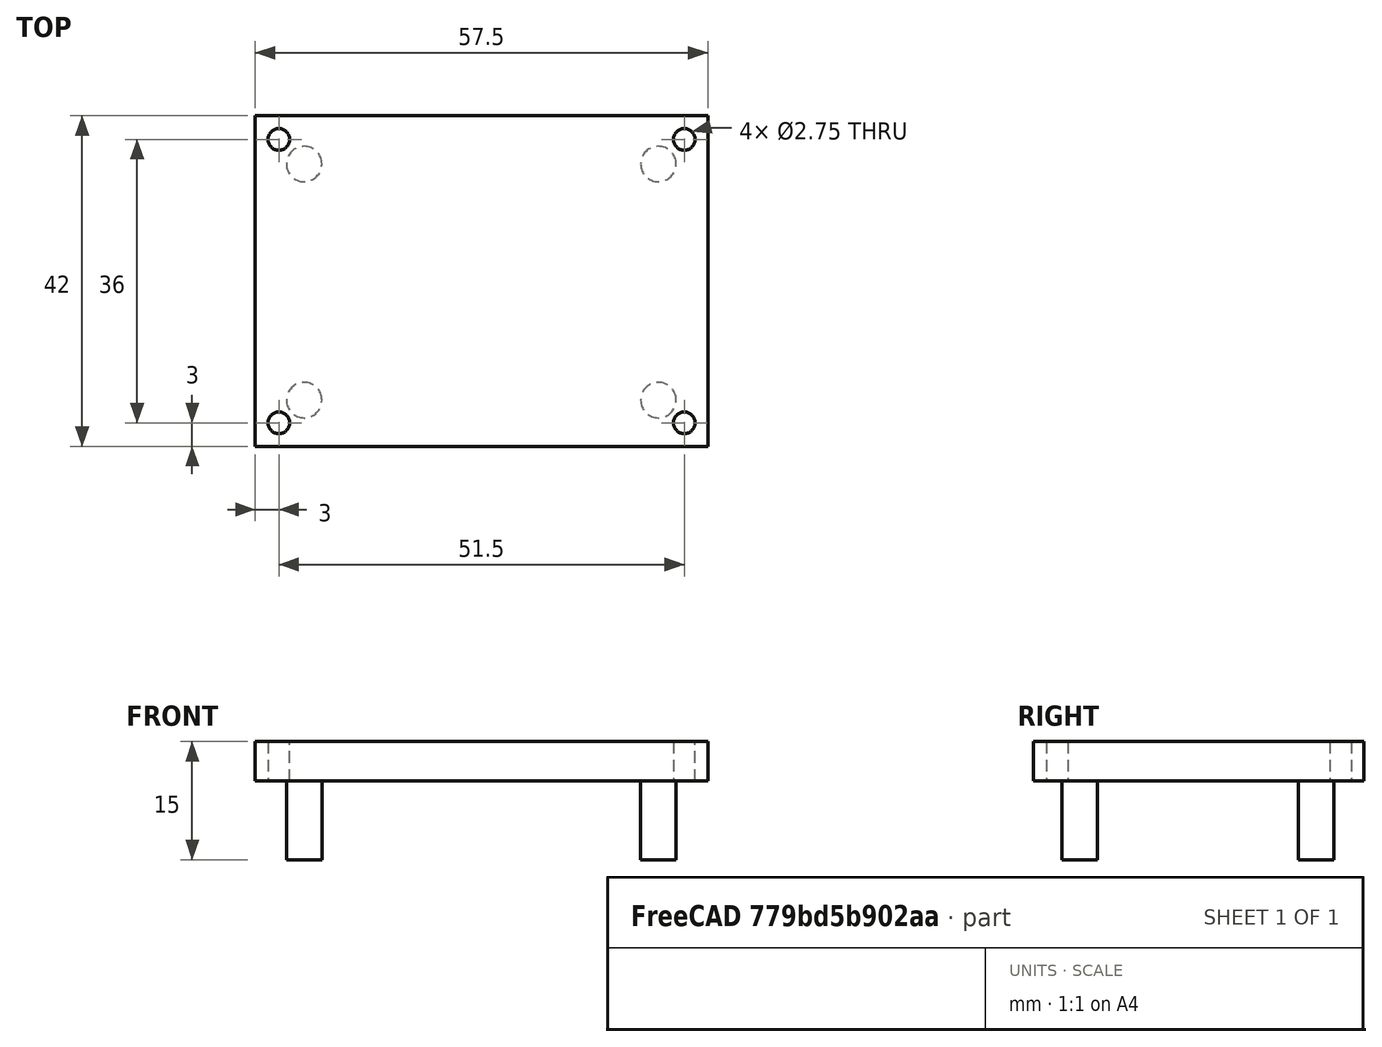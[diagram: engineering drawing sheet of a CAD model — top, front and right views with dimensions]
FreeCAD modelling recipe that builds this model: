
FCSTD DOCUMENT  (FreeCAD 1.0R39109 (Git))
Label: powerplate
License: All rights reserved
LicenseURL: https://en.wikipedia.org/wiki/All_rights_reserved
objects: Sketcher::SketchObject×2, Part::Extrusion×2, Part::Box×1, Part::Cut×1, Part::Fuse×1, Mesh::Feature×1
note: 9 computed .brp shape members not serialized (recipe doc carries the construction recipe); baked Part::Feature solids carry a one-line shape summary decoded from their .brp

FEATURE [Part::Box] Box  label="Base"
  AttacherType = Attacher::AttachEngine3D
  Height = 5
  Length = 57.5
  Width = 42
FEATURE [Sketcher::SketchObject] Sketch  label="Sketch-Screwholes"
  ArcFitTolerance = 1e-06
  AttachmentSupport = -> [Box]
  ExternalGeometry = -> [Box]
  FullyConstrained = true
  MakeInternals = false
  MapMode = 5
  Placement = pos=(0,0,5) rot=(0,0,1;0rad)
  sketch-geometry (4):
    g0: Circle CenterX=3 CenterY=39 CenterZ=0 NormalX=0 NormalY=0 NormalZ=1 AngleXU=0 Radius=1.375
    g1: Circle CenterX=54.5 CenterY=39 CenterZ=0 NormalX=0 NormalY=0 NormalZ=1 AngleXU=0 Radius=1.375
    g2: Circle CenterX=54.5 CenterY=3 CenterZ=0 NormalX=0 NormalY=0 NormalZ=1 AngleXU=0 Radius=1.375
    g3: Circle CenterX=3 CenterY=3 CenterZ=0 NormalX=0 NormalY=0 NormalZ=1 AngleXU=0 Radius=1.375
  constraints (12):
    c: Diameter(g0) = 2.75
    c: Diameter(g1) = 2.75
    c: Diameter(g2) = 2.75
    c: Diameter(g3) = 2.75
    c: Distance(g3,g-6) = 3
    c: Distance(g2,g-6) = 3
    c: Distance(g0,g-3) = 3
    c: Distance(g1,g-3) = 3
    c: Distance(g0,g-5) = 3
    c: Distance(g3,g-5) = 3
    c: Distance(g2,g-4) = 3
    c: Distance(g1,g-4) = 3
FEATURE [Part::Extrusion] Extrude  label="Screwholes-Negative"
  Base = -> Sketch
  Dir = (0,0,1)
  DirMode = 2
  FaceMakerClass = Part::FaceMakerBullseye
  FaceMakerMode = 3
  LengthFwd = 0
  LengthRev = 5
  Solid = true
  Symmetric = false
FEATURE [Part::Cut] Cut  label="Base-Screwholes"
  Base = -> Box
  Tool = -> Extrude
FEATURE [Sketcher::SketchObject] Sketch001  label="Sketch-Extensions"
  ArcFitTolerance = 1e-06
  AttachmentSupport = -> [Cut]
  ExternalGeometry = -> [Cut]
  FullyConstrained = true
  MakeInternals = false
  MapMode = 5
  Placement = pos=(0,0,0) rot=(1,0,0;3.14159rad)
  sketch-geometry (6):
    g0: Circle CenterX=51.2157 CenterY=-35.88 CenterZ=0 NormalX=0 NormalY=0 NormalZ=1 AngleXU=0 Radius=2.25
    g1: Circle CenterX=6.21568 CenterY=-35.88 CenterZ=0 NormalX=0 NormalY=0 NormalZ=1 AngleXU=0 Radius=2.25
    g2: Circle CenterX=6.21568 CenterY=-5.88003 CenterZ=0 NormalX=0 NormalY=0 NormalZ=1 AngleXU=0 Radius=2.25
    g3: Circle CenterX=51.2157 CenterY=-5.88003 CenterZ=0 NormalX=0 NormalY=0 NormalZ=1 AngleXU=0 Radius=2.25
    g4: LineSegment [constr] StartX=6.21568 StartY=-35.88 StartZ=0 EndX=51.2157 EndY=-35.88 EndZ=0
    g5: LineSegment [constr] StartX=6.21568 StartY=-35.88 StartZ=0 EndX=6.21568 EndY=-5.88003 EndZ=0
  constraints (15):
    c: Diameter(g3) = 4.5
    c: Diameter(g2) = 4.5
    c: Diameter(g1) = 4.5
    c: Diameter(g0) = 4.5
    c: DistanceY(g1,g2) = 30
    c: DistanceY(g0,g3) = 30
    c: DistanceX(g1,g0) = 45
    c: DistanceX(g2,g3) = 45
    c: Coincident(g4,g1)
    c: Coincident(g4,g0)
    c: Horizontal(g4)
    c: Coincident(g5,g1)
    c: Coincident(g5,g2)
    c: Vertical(g5)
    c: Block(g2)
FEATURE [Part::Extrusion] Extrude001  label="Extensions"
  Base = -> Sketch001
  Dir = (0,0,-1)
  DirMode = 2
  FaceMakerClass = Part::FaceMakerBullseye
  FaceMakerMode = 3
  LengthFwd = 10
  LengthRev = 0
  Solid = true
  Symmetric = false
FEATURE [Part::Fuse] Fusion  label="Base-final"
  Base = -> Cut
  Tool = -> Extrude001
FEATURE [Mesh::Feature] Mesh  label="Base-final (Meshed)"
